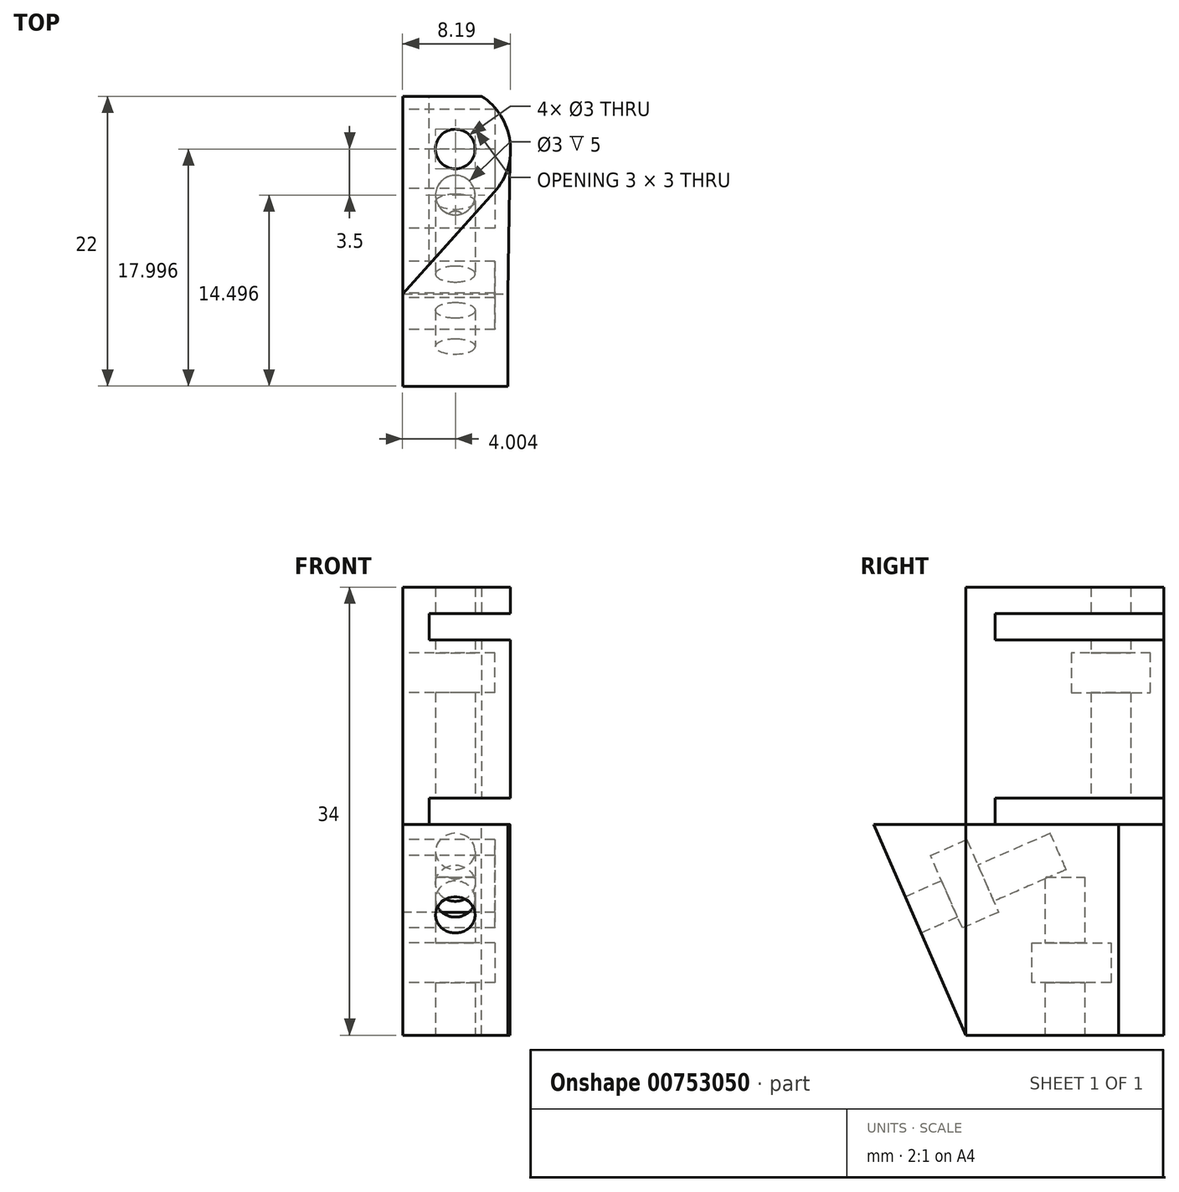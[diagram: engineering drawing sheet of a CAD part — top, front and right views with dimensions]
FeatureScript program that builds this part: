
annotation { "Feature Type Name" : "Feature", "Feature Type Description" : "" }
export const myFeature = defineFeature(function(context is Context, id is Id, definition is map)
    precondition{}
    {
        {
            var Q0;
            Q0=qCreatedBy(makeId("Top.planeOp"),FACE);
            var sketch = newSketch(context, id + "F0", { "sketchPlane" : qUnion([Q0])});
            skLineSegment(sketch, "E0", {"start": v(-26.19, -5.95) * mm, "end": v(-26.19, -20.95) * mm});
            skLineSegment(sketch, "E1", {"start": v(-26.19, -5.95) * mm, "end": v(-20.2, -5.95) * mm});
            skLineSegment(sketch, "E2", {"start": v(-26.19, -20.95) * mm, "end": v(-26.19, -14.95) * mm});
            skLineSegment(sketch, "E3", {"start": v(-26.19, -20.95) * mm, "end": v(-19.23, -13.23) * mm});
            skArc(sketch, "E4", {"start": v(-19.23, -13.23) * mm, "mid": v(-18.04, -9.37) * mm, "end": v(-20.2, -5.95) * mm});
            skCircle(sketch, "E5", {"center": v(-22.19, -9.95) * mm, "radius": 1.5 * mm});
            skSolve(sketch);
        }
        {
            var Q0;
            Q0=makeQuery(id+"F0.imprint","IMPRINT",FACE,{"disambiguationData":[TD([[makeQuery(id+"F0.imprint","IMPRINT",EDGE,{"derivedFrom":sQuery(id+"F0.wireOp",EDGE,"E0")}),1.0]])]});
            extrude(context, id + "F1", {"entities" : qUnion([Q0]), "depth" : 18 * mm, "offsetDistance" : 25 * mm});
        }
        {
            var Q0;
            Q0=makeQuery(id+"F1.opExtrude","SWEPT_FACE",FACE,{"disambiguationData":[OSD([sQuery(id+"F0.wireOp",EDGE,"E0"),sQuery(id+"F0.wireOp",EDGE,"E2")])]});
            var sketch = newSketch(context, id + "F2", { "sketchPlane" : qUnion([Q0])});
            skLineSegment(sketch, "E6", {"start": v(6.95, 13) * mm, "end": v(12.95, 13) * mm});
            skLineSegment(sketch, "E7", {"start": v(12.95, 13) * mm, "end": v(12.95, 10) * mm});
            skLineSegment(sketch, "E8", {"start": v(12.95, 10) * mm, "end": v(6.95, 10) * mm});
            skLineSegment(sketch, "E9", {"start": v(6.95, 10) * mm, "end": v(6.95, 13) * mm});
            skSolve(sketch);
        }
        {
            var Q0;
            Q0=makeQuery(id+"F2.imprint","IMPRINT",FACE,{"disambiguationData":[TD([[makeQuery(id+"F2.imprint","IMPRINT",EDGE,{"derivedFrom":sQuery(id+"F2.wireOp",EDGE,"E6")}),-1.0]])]});
            extrude(context, id + "F3", {"entities" : qUnion([Q0]), "operationType" : NewBodyOperationType.REMOVE, "oppositeDirection" : true, "depth" : 7 * mm, "offsetDistance" : 25 * mm});
        }
        {
            var Q0;
            Q0=makeQuery(id+"F1.opExtrude","CAP_FACE",FACE,{"disambiguationData":[OSD([sQuery(id+"F0.wireOp",EDGE,"E0"),sQuery(id+"F0.wireOp",EDGE,"E1"),sQuery(id+"F0.wireOp",EDGE,"E2"),sQuery(id+"F0.wireOp",EDGE,"E3"),sQuery(id+"F0.wireOp",EDGE,"E4"),sQuery(id+"F0.wireOp",EDGE,"E5")])],"isStart":true});
            var sketch = newSketch(context, id + "F4", { "sketchPlane" : qUnion([Q0])});
            skLineSegment(sketch, "E10", {"start": v(-26.19, 20.95) * mm, "end": v(-18.19, 20.95) * mm});
            skPoint(sketch, "E11.endSnap0", {"position": v(-18.04, 9.37) * mm});
            skLineSegment(sketch, "E12", {"start": v(-26.19, 20.95) * mm, "end": v(-26.19, 5.95) * mm});
            skLineSegment(sketch, "E13", {"start": v(-26.19, 5.95) * mm, "end": v(-20.2, 5.95) * mm});
            skArc(sketch, "E14", {"start": v(-20.2, 5.95) * mm, "mid": v(-18.74, 7.43) * mm, "end": v(-18.04, 9.37) * mm});
            skLineSegment(sketch, "E15", {"start": v(-18.19, 20.95) * mm, "end": v(-18.04, 9.37) * mm});
            skSolve(sketch);
        }
        {
            var Q0;
            Q0=makeQuery(id+"F4.imprint","IMPRINT",FACE,{"disambiguationData":[TD([[makeQuery(id+"F4.imprint","IMPRINT",EDGE,{"derivedFrom":sQuery(id+"F4.wireOp",EDGE,"E12")}),-1.0]])]});
            var Q1;
            {var subQ0=sQuery(id+"F4.wireOp",EDGE,"E10");Q1=makeQuery(id+"F4.imprint","IMPRINT",FACE,{"disambiguationData":[TD([[makeQuery(id+"F4.imprint","IMPRINT",EDGE,{"derivedFrom":subQ0}),-1.0]])]});}
            extrude(context, id + "F5", {"entities" : qUnion([Q0, Q1]), "operationType" : NewBodyOperationType.ADD, "depth" : 16 * mm, "offsetDistance" : 25 * mm});
        }
        {
            var Q0;
            Q0=makeQuery(id+"F5.opExtrude","CAP_FACE",FACE,{"disambiguationData":[OSD([sQuery(id+"F0.wireOp",EDGE,"E5"),sQuery(id+"F4.wireOp",EDGE,"E10"),sQuery(id+"F4.wireOp",EDGE,"E12"),sQuery(id+"F4.wireOp",EDGE,"E13"),sQuery(id+"F4.wireOp",EDGE,"E14"),sQuery(id+"F4.wireOp",EDGE,"E15")])],"isStart":false});
            var sketch = newSketch(context, id + "F6", { "sketchPlane" : qUnion([Q0])});
            skCircle(sketch, "E16", {"center": v(-22.19, 9.95) * mm, "radius": 1.5 * mm});
            skSolve(sketch);
        }
        {
            var Q0;
            Q0 = qSketchRegion(id + "F6", true);
            extrude(context, id + "F7", {"entities" : qUnion([Q0]), "operationType" : NewBodyOperationType.ADD, "depth" : -16 * mm, "offsetDistance" : 25 * mm});
        }
        {
            var Q0;
            Q0=makeQuery(id+"F5.boolean.opBoolean","MERGE",FACE,{"derivedFrom":[makeQuery(id+"F1.opExtrude","SWEPT_FACE",FACE,{"disambiguationData":[OSD([sQuery(id+"F0.wireOp",EDGE,"E0"),sQuery(id+"F0.wireOp",EDGE,"E2")])]}),makeQuery(id+"F5.opExtrude","SWEPT_FACE",FACE,{"disambiguationData":[OSD([sQuery(id+"F4.wireOp",EDGE,"E12")])]})]});
            var sketch = newSketch(context, id + "F8", { "sketchPlane" : qUnion([Q0])});
            skLineSegment(sketch, "E17", {"start": v(20.95, -16) * mm, "end": v(20.95, 0) * mm});
            skLineSegment(sketch, "E18", {"start": v(20.95, 0) * mm, "end": v(27.95, 0) * mm});
            skLineSegment(sketch, "E19", {"start": v(27.95, 0) * mm, "end": v(20.95, -16) * mm});
            skSolve(sketch);
        }
        {
            var Q0;
            Q0=makeQuery(id+"F8.imprint","IMPRINT",FACE,{"disambiguationData":[TD([[makeQuery(id+"F8.imprint","IMPRINT",EDGE,{"derivedFrom":sQuery(id+"F8.wireOp",EDGE,"E17")}),-1.0]])]});
            extrude(context, id + "F9", {"entities" : qUnion([Q0]), "operationType" : NewBodyOperationType.ADD, "depth" : -8 * mm, "offsetDistance" : 25 * mm});
        }
        {
            var Q0;
            Q0=makeQuery(id+"F9.boolean.opBoolean","MERGE",FACE,{"derivedFrom":[makeQuery(id+"F5.boolean.opBoolean","MERGE",FACE,{"derivedFrom":[makeQuery(id+"F1.opExtrude","SWEPT_FACE",FACE,{"disambiguationData":[OSD([sQuery(id+"F0.wireOp",EDGE,"E0"),sQuery(id+"F0.wireOp",EDGE,"E2")])]}),makeQuery(id+"F5.opExtrude","SWEPT_FACE",FACE,{"disambiguationData":[OSD([sQuery(id+"F4.wireOp",EDGE,"E12")])]})]}),makeQuery(id+"F9.opExtrude","CAP_FACE",FACE,{"disambiguationData":[OSD([sQuery(id+"F8.wireOp",EDGE,"E17"),sQuery(id+"F8.wireOp",EDGE,"E18"),sQuery(id+"F8.wireOp",EDGE,"E19")])],"isStart":true})]});
            var sketch = newSketch(context, id + "F10", { "sketchPlane" : qUnion([Q0])});
            skLineSegment(sketch, "E20", {"start": v(23.64, -2.37) * mm, "end": v(20.9, -1.17) * mm});
            skLineSegment(sketch, "E21", {"start": v(20.9, -1.17) * mm, "end": v(18.48, -6.66) * mm});
            skLineSegment(sketch, "E22", {"start": v(18.48, -6.66) * mm, "end": v(21.23, -7.87) * mm});
            skLineSegment(sketch, "E23", {"start": v(21.23, -7.87) * mm, "end": v(23.64, -2.37) * mm});
            skSolve(sketch);
        }
        {
            var Q0;
            Q0=makeQuery(id+"F10.imprint","IMPRINT",FACE,{"disambiguationData":[TD([[makeQuery(id+"F10.imprint","IMPRINT",EDGE,{"derivedFrom":sQuery(id+"F10.wireOp",EDGE,"E20")}),1.0]])]});
            extrude(context, id + "F11", {"entities" : qUnion([Q0]), "operationType" : NewBodyOperationType.REMOVE, "oppositeDirection" : true, "depth" : 7 * mm, "offsetDistance" : 25 * mm});
        }
        {
            var Q0;
            Q0=makeQuery(id+"F9.opExtrude","SWEPT_FACE",FACE,{"disambiguationData":[OSD([sQuery(id+"F8.wireOp",EDGE,"E19")])]});
            var sketch = newSketch(context, id + "F12", { "sketchPlane" : qUnion([Q0])});
            skCircle(sketch, "E24", {"center": v(-22.19, 3.7) * mm, "radius": 1.5 * mm});
            skSolve(sketch);
        }
        {
            var Q0;
            Q0=makeQuery(id+"F12.imprint","IMPRINT",FACE,{"disambiguationData":[TD([[makeQuery(id+"F12.imprint","IMPRINT",EDGE,{"derivedFrom":sQuery(id+"F12.wireOp",EDGE,"E24")}),1.0]])]});
            extrude(context, id + "F13", {"entities" : qUnion([Q0]), "operationType" : NewBodyOperationType.REMOVE, "oppositeDirection" : true, "depth" : 12 * mm, "offsetDistance" : 25 * mm});
        }
        {
            var Q0;
            Q0=makeQuery(id+"F9.boolean.opBoolean","MERGE",FACE,{"derivedFrom":[makeQuery(id+"F5.boolean.opBoolean","MERGE",FACE,{"derivedFrom":[makeQuery(id+"F1.opExtrude","SWEPT_FACE",FACE,{"disambiguationData":[OSD([sQuery(id+"F0.wireOp",EDGE,"E0"),sQuery(id+"F0.wireOp",EDGE,"E2")])]}),makeQuery(id+"F5.opExtrude","SWEPT_FACE",FACE,{"disambiguationData":[OSD([sQuery(id+"F4.wireOp",EDGE,"E12")])]})]}),makeQuery(id+"F9.opExtrude","CAP_FACE",FACE,{"disambiguationData":[OSD([sQuery(id+"F8.wireOp",EDGE,"E17"),sQuery(id+"F8.wireOp",EDGE,"E18"),sQuery(id+"F8.wireOp",EDGE,"E19")])],"isStart":true})]});
            var sketch = newSketch(context, id + "F14", { "sketchPlane" : qUnion([Q0])});
            skLineSegment(sketch, "E25", {"start": v(9.95, -12) * mm, "end": v(15.95, -12) * mm});
            skLineSegment(sketch, "E26", {"start": v(15.95, -12) * mm, "end": v(15.95, -9) * mm});
            skLineSegment(sketch, "E27", {"start": v(15.95, -9) * mm, "end": v(9.95, -9) * mm});
            skLineSegment(sketch, "E28", {"start": v(9.95, -9) * mm, "end": v(9.95, -12) * mm});
            skSolve(sketch);
        }
        {
            var Q0;
            Q0=makeQuery(id+"F14.imprint","IMPRINT",FACE,{"disambiguationData":[TD([[makeQuery(id+"F14.imprint","IMPRINT",EDGE,{"derivedFrom":sQuery(id+"F14.wireOp",EDGE,"E25")}),1.0]])]});
            extrude(context, id + "F15", {"entities" : qUnion([Q0]), "operationType" : NewBodyOperationType.REMOVE, "oppositeDirection" : true, "depth" : 7 * mm, "offsetDistance" : 25 * mm});
        }
        {
            var Q0;
            Q0=makeQuery(id+"F7.boolean.opBoolean","MERGE",FACE,{"derivedFrom":[makeQuery(id+"F5.opExtrude","CAP_FACE",FACE,{"disambiguationData":[OSD([sQuery(id+"F0.wireOp",EDGE,"E5"),sQuery(id+"F4.wireOp",EDGE,"E10"),sQuery(id+"F4.wireOp",EDGE,"E12"),sQuery(id+"F4.wireOp",EDGE,"E13"),sQuery(id+"F4.wireOp",EDGE,"E14"),sQuery(id+"F4.wireOp",EDGE,"E15")])],"isStart":false}),makeQuery(id+"F7.opExtrude","CAP_FACE",FACE,{"disambiguationData":[OSD([sQuery(id+"F6.wireOp",EDGE,"E16")])],"isStart":true})]});
            var sketch = newSketch(context, id + "F16", { "sketchPlane" : qUnion([Q0])});
            skCircle(sketch, "E29", {"center": v(-22.19, 13.45) * mm, "radius": 1.5 * mm});
            skSolve(sketch);
        }
        {
            var Q0;
            Q0=makeQuery(id+"F16.imprint","IMPRINT",FACE,{"disambiguationData":[TD([[makeQuery(id+"F16.imprint","IMPRINT",EDGE,{"derivedFrom":sQuery(id+"F16.wireOp",EDGE,"E29")}),1.0]])]});
            extrude(context, id + "F17", {"entities" : qUnion([Q0]), "operationType" : NewBodyOperationType.REMOVE, "oppositeDirection" : true, "depth" : 12 * mm, "offsetDistance" : 25 * mm});
        }
        {
            var Q0;
            Q0=makeQuery(id+"F5.boolean.opBoolean","MERGE",FACE,{"derivedFrom":[makeQuery(id+"F1.opExtrude","SWEPT_FACE",FACE,{"disambiguationData":[OSD([sQuery(id+"F0.wireOp",EDGE,"E1")])]}),makeQuery(id+"F5.opExtrude","SWEPT_FACE",FACE,{"disambiguationData":[OSD([sQuery(id+"F4.wireOp",EDGE,"E13")])]})]});
            var sketch = newSketch(context, id + "F18", { "sketchPlane" : qUnion([Q0])});
            skLineSegment(sketch, "E30", {"start": v(26.19, 0) * mm, "end": v(24.19, 0) * mm});
            skLineSegment(sketch, "E31", {"start": v(24.19, 0) * mm, "end": v(24.19, 2) * mm});
            skLineSegment(sketch, "E32", {"start": v(24.19, 2) * mm, "end": v(26.19, 2) * mm});
            skLineSegment(sketch, "E33", {"start": v(24.19, 2) * mm, "end": v(20.2, 2) * mm});
            skLineSegment(sketch, "E34", {"start": v(20.2, 2) * mm, "end": v(20.2, 0) * mm});
            skLineSegment(sketch, "E35", {"start": v(20.2, 0) * mm, "end": v(24.19, 0) * mm});
            skSolve(sketch);
        }
        {
            var Q0;
            Q0=makeQuery(id+"F18.imprint","IMPRINT",FACE,{"disambiguationData":[TD([[makeQuery(id+"F18.imprint","IMPRINT",EDGE,{"derivedFrom":sQuery(id+"F18.wireOp",EDGE,"E31")}),1.0]])]});
            extrude(context, id + "F19", {"entities" : qUnion([Q0]), "operationType" : NewBodyOperationType.REMOVE, "oppositeDirection" : true, "depth" : 25 * mm, "offsetDistance" : 25 * mm});
        }
        {
            var Q0;
            Q0=makeQuery(id+"F19.boolean.opBoolean","COPY",FACE,{"derivedFrom":makeQuery(id+"F19.opExtrude","SWEPT_FACE",FACE,{"disambiguationData":[OSD([sQuery(id+"F18.wireOp",EDGE,"E34")])]})});
            extrude(context, id + "F20", {"entities" : qUnion([Q0]), "operationType" : NewBodyOperationType.REMOVE, "oppositeDirection" : true, "depth" : 25 * mm, "offsetDistance" : 25 * mm});
        }
        {
            var Q0;
            Q0=makeQuery(id+"F5.boolean.opBoolean","MERGE",FACE,{"derivedFrom":[makeQuery(id+"F1.opExtrude","SWEPT_FACE",FACE,{"disambiguationData":[OSD([sQuery(id+"F0.wireOp",EDGE,"E1")])]}),makeQuery(id+"F5.opExtrude","SWEPT_FACE",FACE,{"disambiguationData":[OSD([sQuery(id+"F4.wireOp",EDGE,"E13")])]})]});
            var sketch = newSketch(context, id + "F21", { "sketchPlane" : qUnion([Q0])});
            skLineSegment(sketch, "E36", {"start": v(26.19, 18) * mm, "end": v(26.19, 16) * mm});
            skLineSegment(sketch, "E37", {"start": v(26.19, 16) * mm, "end": v(26.19, 14) * mm});
            skLineSegment(sketch, "E38", {"start": v(26.19, 14) * mm, "end": v(24.19, 14) * mm});
            skLineSegment(sketch, "E39", {"start": v(24.19, 14) * mm, "end": v(20.2, 14) * mm});
            skLineSegment(sketch, "E40", {"start": v(20.2, 14) * mm, "end": v(20.2, 16) * mm});
            skLineSegment(sketch, "E41", {"start": v(20.2, 16) * mm, "end": v(26.19, 16) * mm});
            skLineSegment(sketch, "E42", {"start": v(24.19, 16) * mm, "end": v(24.19, 14) * mm});
            skSolve(sketch);
        }
        {
            var Q0;
            Q0=makeQuery(id+"F21.imprint","IMPRINT",FACE,{"disambiguationData":[TD([[makeQuery(id+"F21.imprint","IMPRINT",EDGE,{"derivedFrom":sQuery(id+"F21.wireOp",EDGE,"E39")}),-1.0]])]});
            extrude(context, id + "F22", {"entities" : qUnion([Q0]), "operationType" : NewBodyOperationType.REMOVE, "oppositeDirection" : true, "depth" : 25 * mm, "offsetDistance" : 25 * mm});
        }
        {
            var Q0;
            Q0=makeQuery(id+"F22.boolean.opBoolean","COPY",FACE,{"derivedFrom":makeQuery(id+"F22.opExtrude","SWEPT_FACE",FACE,{"disambiguationData":[OSD([sQuery(id+"F21.wireOp",EDGE,"E40")])]})});
            extrude(context, id + "F23", {"entities" : qUnion([Q0]), "operationType" : NewBodyOperationType.REMOVE, "oppositeDirection" : true, "depth" : 25 * mm, "offsetDistance" : 25 * mm});
        }
    });
